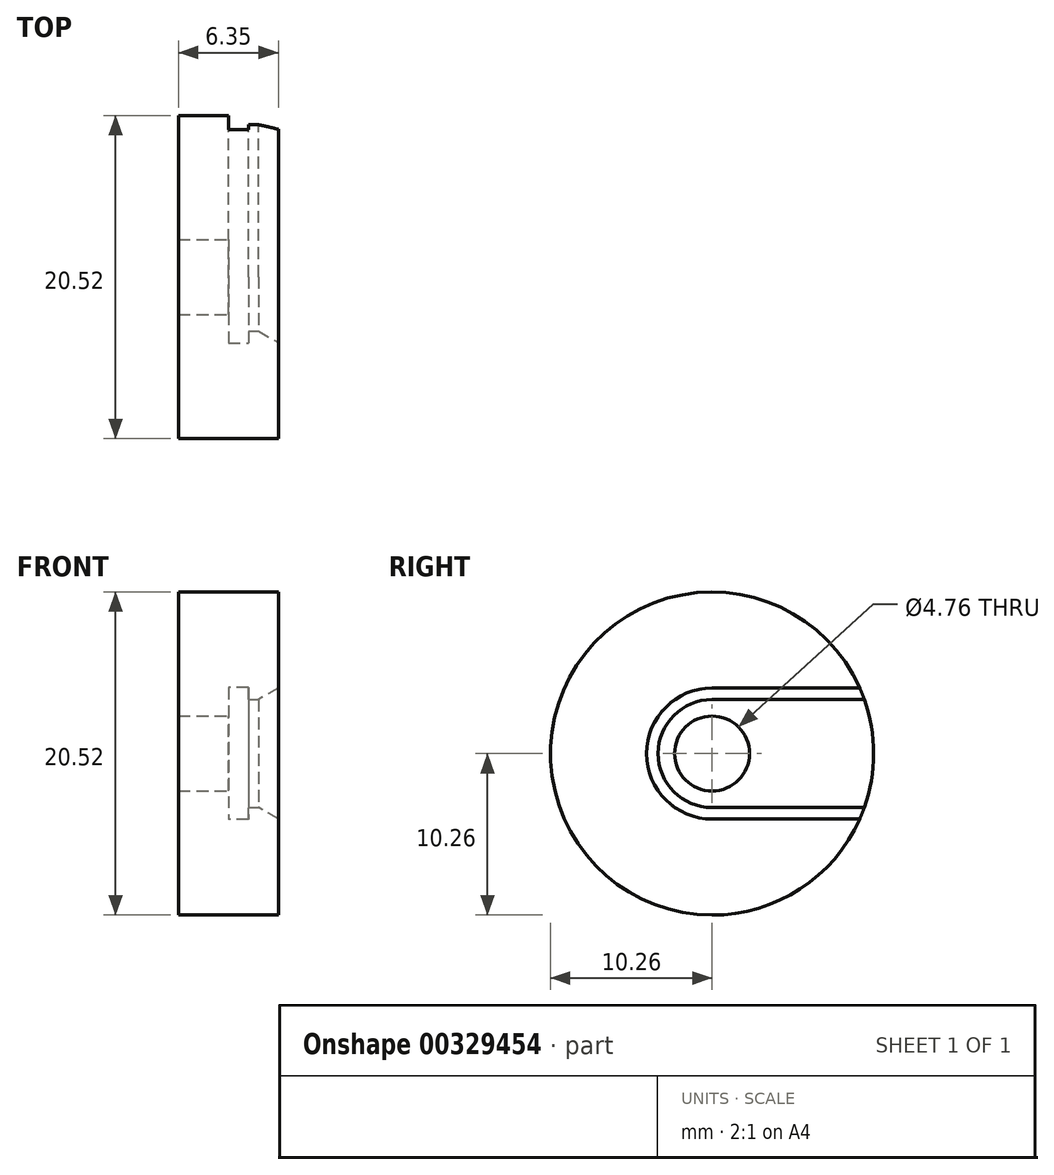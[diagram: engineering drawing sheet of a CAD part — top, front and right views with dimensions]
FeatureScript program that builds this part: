
annotation { "Feature Type Name" : "Feature", "Feature Type Description" : "" }
export const myFeature = defineFeature(function(context is Context, id is Id, definition is map)
    precondition{}
    {
        {
            var Q0;
            Q0=qCreatedBy(makeId("Top.planeOp"),FACE);
            var sketch = newSketch(context, id + "F0", { "sketchPlane" : qUnion([Q0])});
            skLineSegment(sketch, "E0.bottom", {"start": v(0, 0) * mm, "end": v(-6.35, 0) * mm});
            skLineSegment(sketch, "E0.top", {"start": v(0, 10.26) * mm, "end": v(-6.35, 10.26) * mm});
            skLineSegment(sketch, "E0.left", {"start": v(0, 3.43) * mm, "end": v(0, 10.26) * mm});
            skLineSegment(sketch, "E0.right", {"start": v(-6.35, 2.38) * mm, "end": v(-6.35, 10.26) * mm});
            skLineSegment(sketch, "E1", {"start": v(-1.9, 3.43) * mm, "end": v(-1.9, 4.2) * mm});
            skLineSegment(sketch, "E2", {"start": v(-1.9, 4.2) * mm, "end": v(-3.17, 4.2) * mm});
            skLineSegment(sketch, "E3", {"start": v(-3.17, 4.2) * mm, "end": v(-3.17, 2.38) * mm});
            skLineSegment(sketch, "E4", {"start": v(-3.17, 2.38) * mm, "end": v(-6.35, 2.38) * mm});
            skLineSegment(sketch, "E5", {"start": v(-1.9, 3.43) * mm, "end": v(0, 3.43) * mm});
            skSolve(sketch);
        }
        {
            var Q0;
            Q0 = qSketchRegion(id + "F0", true);
            var Q1;
            Q1=sQuery(id+"F0.wireOp",EDGE,"E0.bottom");
            revolve(context, id + "F1", {"entities" : qUnion([Q0]), "axis" : qUnion([Q1]), "revolveType" : RevolveType.FULL});
        }
        {
            var Q0;
            Q0=makeQuery(id+"F1.opRevolve","SWEPT_FACE",FACE,{"disambiguationData":[OSD([sQuery(id+"F0.wireOp",EDGE,"E0.left")])]});
            var sketch = newSketch(context, id + "F2", { "sketchPlane" : qUnion([Q0])});
            skLineSegment(sketch, "E6", {"start": v(0, -3.43) * mm, "end": v(9.67, -3.43) * mm});
            skLineSegment(sketch, "E7", {"start": v(0, 3.43) * mm, "end": v(9.67, 3.43) * mm});
            skCircle(sketch, "E8.0", {"center": v(0, 0) * mm, "radius": 3.43 * mm});
            skCircle(sketch, "E9.0.0", {"center": v(0, 0) * mm, "radius": 10.26 * mm});
            skSolve(sketch);
        }
        {
            var Q0;
            {var subQ0=sQuery(id+"F2.wireOp",EDGE,"E6");Q0=makeQuery(id+"F2.imprint","IMPRINT",FACE,{"disambiguationData":[TD([[makeQuery(id+"F2.imprint","IMPRINT",EDGE,{"derivedFrom":subQ0}),1.0]])]});}
            var Q1;
            Q1=makeQuery(id+"F1.opRevolve","SWEPT_FACE",FACE,{"disambiguationData":[OSD([sQuery(id+"F0.wireOp",EDGE,"E3")])]});
            extrude(context, id + "F3", {"entities" : qUnion([Q0]), "operationType" : NewBodyOperationType.REMOVE, "endBound" : BoundingType.UP_TO_SURFACE, "oppositeDirection" : true, "endBoundEntityFace" : qUnion([Q1]), "depth" : 25.4 * mm});
        }
        {
            var Q0;
            Q0=makeQuery(id+"F3.boolean.opBoolean","MERGE",FACE,{"derivedFrom":[makeQuery(id+"F1.opRevolve","SWEPT_FACE",FACE,{"disambiguationData":[OSD([sQuery(id+"F0.wireOp",EDGE,"E3")])]})],"fromTools":[makeQuery(id+"F3.opExtrude","CAP_FACE",FACE,{"disambiguationData":[OSD([sQuery(id+"F2.wireOp",EDGE,"E6"),sQuery(id+"F2.wireOp",EDGE,"E7"),sQuery(id+"F2.wireOp",EDGE,"E8.0"),sQuery(id+"F2.wireOp",EDGE,"E9.0.0")])],"isStart":false})]});
            var sketch = newSketch(context, id + "F4", { "sketchPlane" : qUnion([Q0])});
            skLineSegment(sketch, "E10", {"start": v(0, -4.2) * mm, "end": v(9.37, -4.2) * mm});
            skLineSegment(sketch, "E11", {"start": v(0, 4.2) * mm, "end": v(9.37, 4.2) * mm});
            skArc(sketch, "E12.0", {"start": v(9.67, -3.43) * mm, "mid": v(10.26, 0) * mm, "end": v(9.67, 3.43) * mm});
            skArc(sketch, "E13.0.0", {"start": v(0, 4.2) * mm, "mid": v(-4.2, 0) * mm, "end": v(0, -4.2) * mm});
            skArc(sketch, "E14.0", {"start": v(9.37, -4.2) * mm, "mid": v(10.26, 0) * mm, "end": v(9.37, 4.2) * mm});
            skSolve(sketch);
        }
        {
            var Q0;
            Q0 = qSketchRegion(id + "F4", true);
            extrude(context, id + "F5", {"entities" : qUnion([Q0]), "operationType" : NewBodyOperationType.REMOVE, "depth" : 1.27 * mm});
        }
        {
            var Q0;
            Q0=makeQuery(id+"F3.boolean.opBoolean","COPY",EDGE,{"derivedFrom":makeQuery(id+"F3.opExtrude","CAP_EDGE",EDGE,{"disambiguationData":[OSD([sQuery(id+"F2.wireOp",EDGE,"E6")])],"isStart":true})});
            var Q1;
            Q1=makeQuery(id+"F1.opRevolve","SWEPT_EDGE",EDGE,{"disambiguationData":[OSD([sQuery(id+"F0.wireOp",EDGE,"E0.left"),sQuery(id+"F0.wireOp",EDGE,"E5")])]});
            var Q2;
            Q2=makeQuery(id+"F3.boolean.opBoolean","COPY",EDGE,{"derivedFrom":makeQuery(id+"F3.opExtrude","CAP_EDGE",EDGE,{"disambiguationData":[OSD([sQuery(id+"F2.wireOp",EDGE,"E7")])],"isStart":true})});
            chamfer(context, id + "F6", {"entities" : qUnion([Q0, Q1, Q2]), "chamferType" : ChamferType.OFFSET_ANGLE, "width" : 1.27 * mm, "oppositeDirection" : false, "angle" : 30 * degree, "tangentPropagation" : true});
        }
    });
